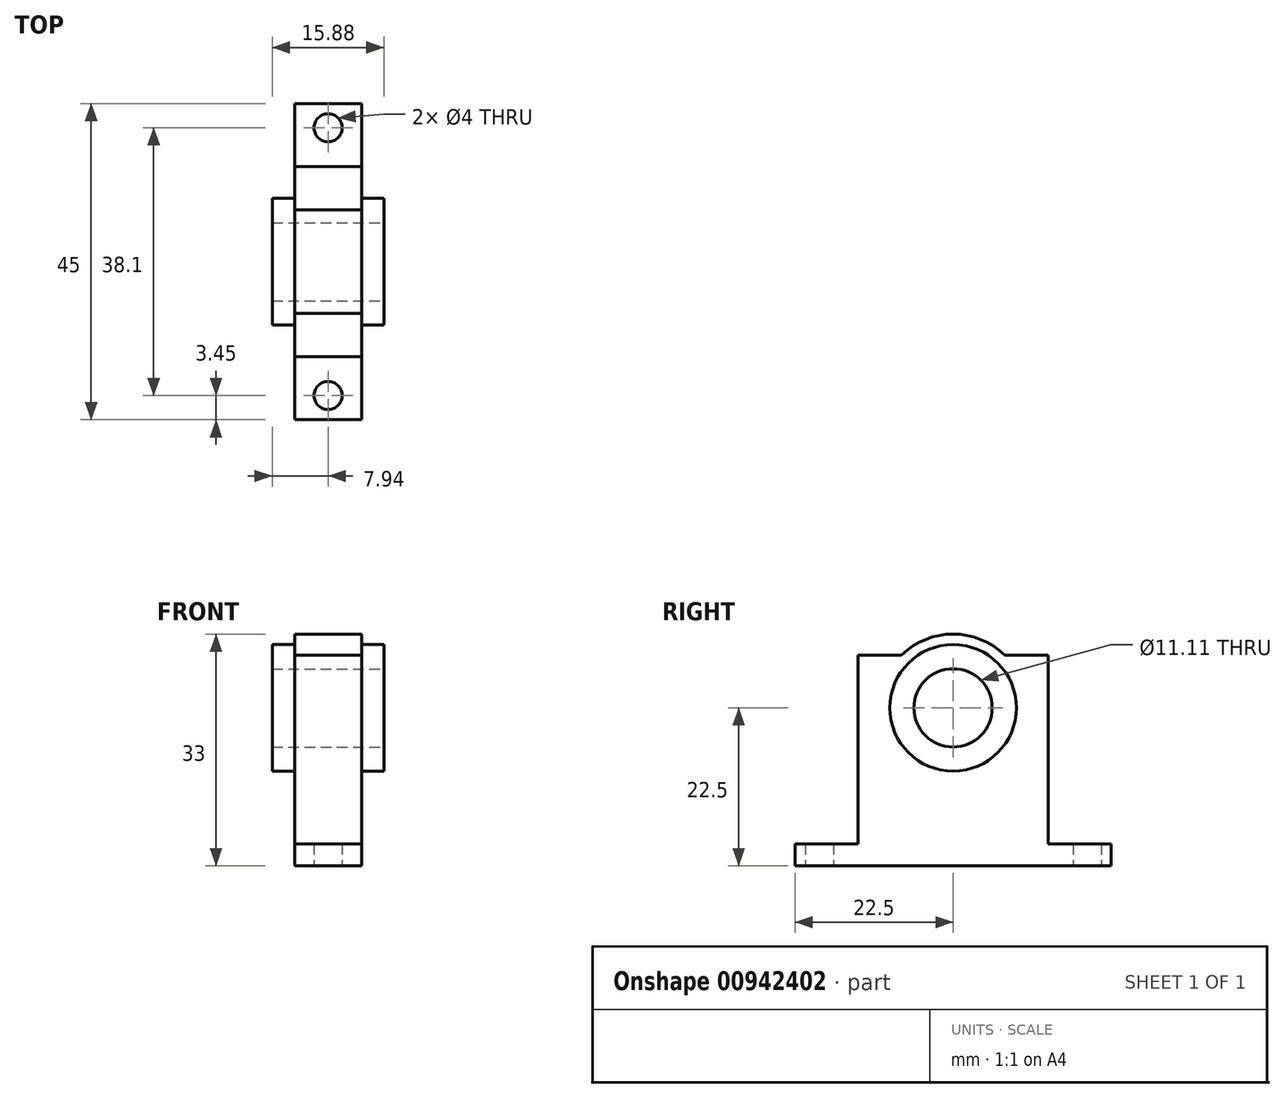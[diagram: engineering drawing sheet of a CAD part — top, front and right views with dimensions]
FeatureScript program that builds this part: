
annotation { "Feature Type Name" : "Feature", "Feature Type Description" : "" }
export const myFeature = defineFeature(function(context is Context, id is Id, definition is map)
    precondition{}
    {
        {
            var Q0;
            Q0=qCreatedBy(makeId("Right.planeOp"),FACE);
            var sketch = newSketch(context, id + "F0", { "sketchPlane" : qUnion([Q0])});
            skLineSegment(sketch, "E0.bottom", {"start": v(-13.5, 30) * mm, "end": v(-7.35, 30) * mm});
            skLineSegment(sketch, "E0.top", {"start": v(-22.5, 0) * mm, "end": v(22.5, 0) * mm});
            skLineSegment(sketch, "E0.left", {"start": v(-13.5, 30) * mm, "end": v(-13.5, 3.12) * mm});
            skLineSegment(sketch, "E0.right", {"start": v(13.5, 30) * mm, "end": v(13.5, 3.12) * mm});
            skLineSegment(sketch, "E1", {"start": v(-22.5, 3.12) * mm, "end": v(-22.5, 0) * mm});
            skLineSegment(sketch, "E2", {"start": v(-22.5, 3.12) * mm, "end": v(-13.5, 3.12) * mm});
            skLineSegment(sketch, "E3", {"start": v(22.5, 3.12) * mm, "end": v(22.5, 0) * mm});
            skPoint(sketch, "E4.orphan", {"position": v(13.5, 0) * mm});
            skLineSegment(sketch, "E5.trimOffspring", {"start": v(13.5, 3.12) * mm, "end": v(22.5, 3.12) * mm});
            skArc(sketch, "E6", {"start": v(7.35, 30) * mm, "mid": v(0, 33) * mm, "end": v(-7.35, 30) * mm});
            skLineSegment(sketch, "E7.trimOffspring", {"start": v(7.35, 30) * mm, "end": v(13.5, 30) * mm});
            skSolve(sketch);
        }
        {
            var Q0;
            Q0 = qSketchRegion(id + "F0", true);
            extrude(context, id + "F1", {"entities" : qUnion([Q0]), "depth" : 4.76 * mm, "offsetDistance" : 25 * mm, "hasSecondDirection" : true, "secondDirectionOppositeDirection" : true, "secondDirectionDepth" : 4.76 * mm});
        }
        {
            var Q0;
            Q0=qCreatedBy(makeId("Right.planeOp"),FACE);
            var sketch = newSketch(context, id + "F2", { "sketchPlane" : qUnion([Q0])});
            skCircle(sketch, "E8", {"center": v(0, 22.5) * mm, "radius": 9 * mm});
            skSolve(sketch);
        }
        {
            var Q0;
            Q0 = qSketchRegion(id + "F2", true);
            extrude(context, id + "F3", {"entities" : qUnion([Q0]), "operationType" : NewBodyOperationType.ADD, "depth" : 7.94 * mm, "offsetDistance" : 25 * mm, "hasSecondDirection" : true, "secondDirectionOppositeDirection" : true, "secondDirectionDepth" : 7.94 * mm});
        }
        {
            var Q0;
            Q0=makeQuery(id+"F3.opExtrude","CAP_FACE",FACE,{"disambiguationData":[OSD([sQuery(id+"F2.wireOp",EDGE,"E8")])],"isStart":false});
            var sketch = newSketch(context, id + "F4", { "sketchPlane" : qUnion([Q0])});
            skCircle(sketch, "E9", {"center": v(0, 22.5) * mm, "radius": 5.56 * mm});
            skSolve(sketch);
        }
        {
            var Q0;
            Q0 = qSketchRegion(id + "F4", true);
            extrude(context, id + "F5", {"entities" : qUnion([Q0]), "operationType" : NewBodyOperationType.REMOVE, "endBound" : BoundingType.THROUGH_ALL, "oppositeDirection" : true, "depth" : 25 * mm, "offsetDistance" : 25 * mm});
        }
        {
            var Q0;
            Q0=makeQuery(id+"F1.opExtrude","SWEPT_FACE",FACE,{"disambiguationData":[OSD([sQuery(id+"F0.wireOp",EDGE,"E0.top")])]});
            var sketch = newSketch(context, id + "F6", { "sketchPlane" : qUnion([Q0])});
            skCircle(sketch, "E10", {"center": v(0, 19.05) * mm, "radius": 2 * mm});
            skCircle(sketch, "E11", {"center": v(0, -19.05) * mm, "radius": 2 * mm});
            skSolve(sketch);
        }
        {
            var Q0;
            Q0 = qSketchRegion(id + "F6", true);
            extrude(context, id + "F7", {"entities" : qUnion([Q0]), "operationType" : NewBodyOperationType.REMOVE, "endBound" : BoundingType.THROUGH_ALL, "oppositeDirection" : true, "depth" : 25 * mm, "offsetDistance" : 25 * mm});
        }
    });
